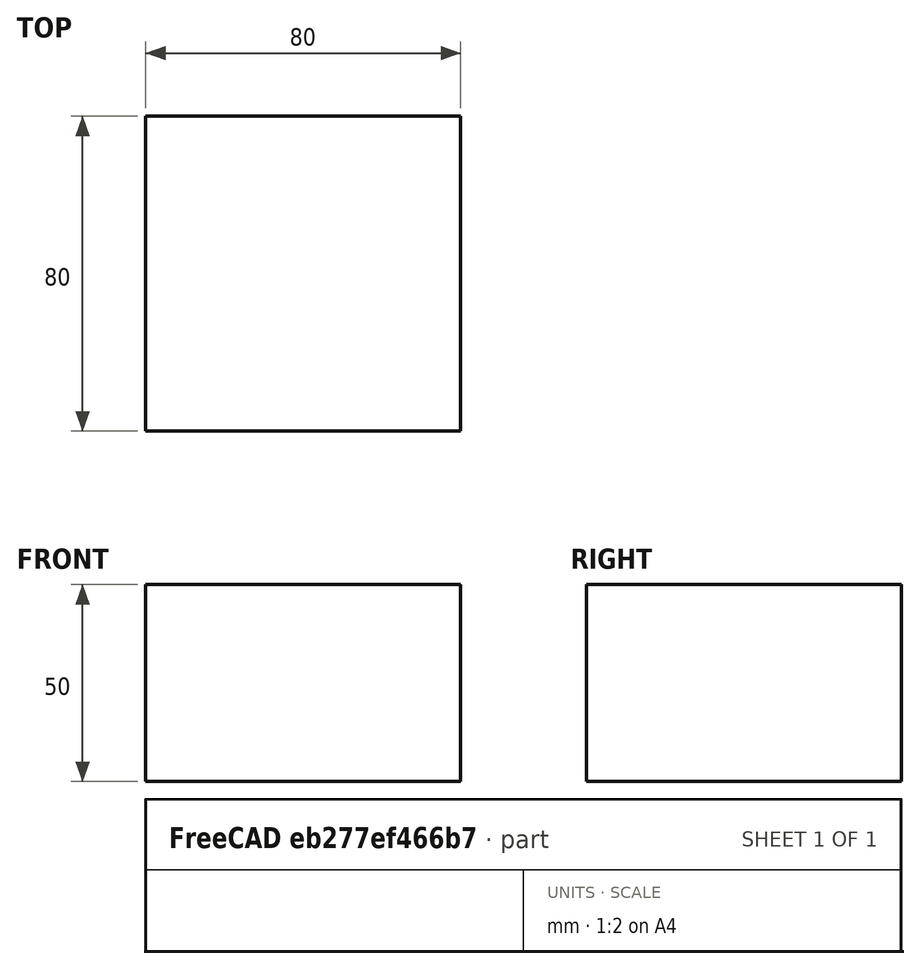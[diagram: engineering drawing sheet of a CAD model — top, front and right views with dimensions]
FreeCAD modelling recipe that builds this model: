
FCSTD DOCUMENT  (FreeCAD 0.15R4671 (Git))
Label: Square Bar 80 EN10059 S235JR
License: All rights reserved
LicenseURL: http://en.wikipedia.org/wiki/All_rights_reserved
objects: Sketcher::SketchObject×1, Part::Extrusion×1
note: 2 computed .brp shape members not serialized (recipe doc carries the construction recipe); baked Part::Feature solids carry a one-line shape summary decoded from their .brp

FEATURE [Sketcher::SketchObject] Sketch
  sketch-geometry (4):
    g0: LineSegment StartX=-40 StartY=-40 StartZ=0 EndX=40 EndY=-40 EndZ=0
    g1: LineSegment StartX=40 StartY=-40 StartZ=0 EndX=40 EndY=40 EndZ=0
    g2: LineSegment StartX=40 StartY=40 StartZ=0 EndX=-40 EndY=40 EndZ=0
    g3: LineSegment StartX=-40 StartY=40 StartZ=0 EndX=-40 EndY=-40 EndZ=0
  constraints (12):
    c: Coincident(g0,g1)
    c: Coincident(g1,g2)
    c: Coincident(g2,g3)
    c: Coincident(g3,g0)
    c: Horizontal(g0)
    c: Horizontal(g2)
    c: Vertical(g1)
    c: Vertical(g3)
    c: Symmetric(g1,g0,g-1)
    c: Symmetric(g2,g1,g-2)
    c: Equal(g1,g2)
    c: DistanceY(g1) = 80
FEATURE [Part::Extrusion] Extrude  label="Square Bar 80 EN10059 S235JR"
  Base = -> Sketch
  Dir = (0,0,50)
  Solid = true
